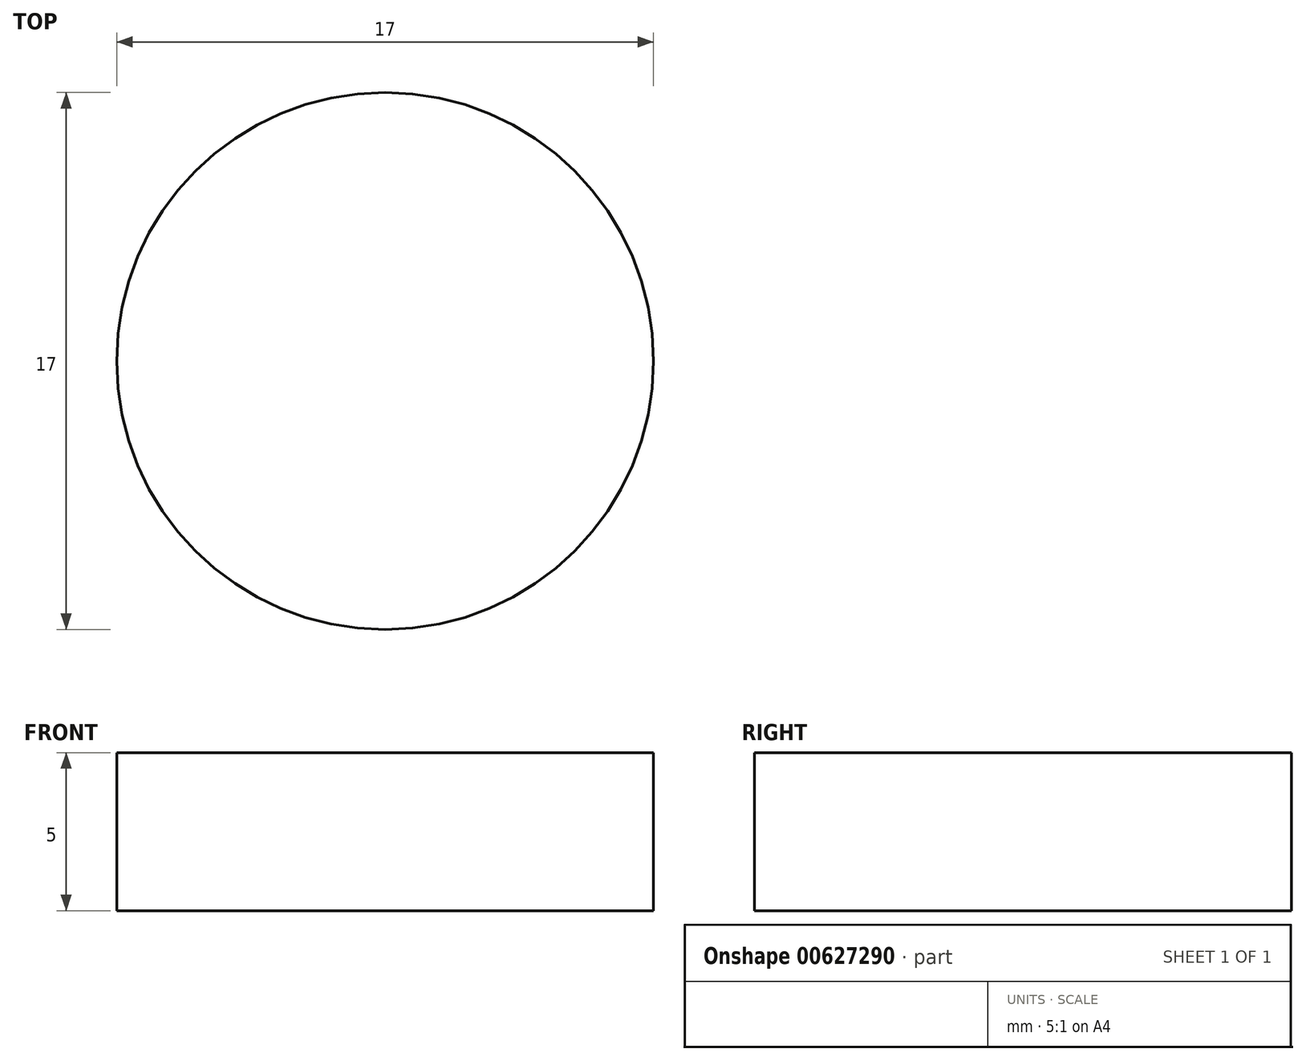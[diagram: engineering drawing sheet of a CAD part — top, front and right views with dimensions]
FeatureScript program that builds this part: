
annotation { "Feature Type Name" : "Feature", "Feature Type Description" : "" }
export const myFeature = defineFeature(function(context is Context, id is Id, definition is map)
    precondition{}
    {
        {
            var Q0;
            Q0=qCreatedBy(makeId("Top.planeOp"),FACE);
            var sketch = newSketch(context, id + "F0", { "sketchPlane" : qUnion([Q0])});
            skArc(sketch, "E0", {"start": v(-4.15, 450.11) * mm, "mid": v(-4.15, 450.11) * mm, "end": v(-4.15, 450.11) * mm});
            skCircle(sketch, "E1.0", {"center": v(0, 0) * mm, "radius": 8.5 * mm});
            skSolve(sketch);
        }
        {
            var Q0;
            Q0=makeQuery(id+"F0.imprint","IMPRINT",FACE,{"disambiguationData":[TD([[makeQuery(id+"F0.imprint","IMPRINT",EDGE,{"derivedFrom":sQuery(id+"F0.wireOp",EDGE,"E1.0")}),1.0]])]});
            extrude(context, id + "F1", {"entities" : qUnion([Q0]), "depth" : 5 * mm, "offsetDistance" : 25 * mm});
        }
        {
            var Q0;
            Q0=sQuery(id+"F0.wireOp",EDGE,"E1.0");
            extrude(context, id + "F2", {"bodyType" : ToolBodyType.SURFACE, "surfaceEntities" : qUnion([Q0]), "depth" : 75 * mm, "offsetDistance" : 25 * mm});
        }
    });
